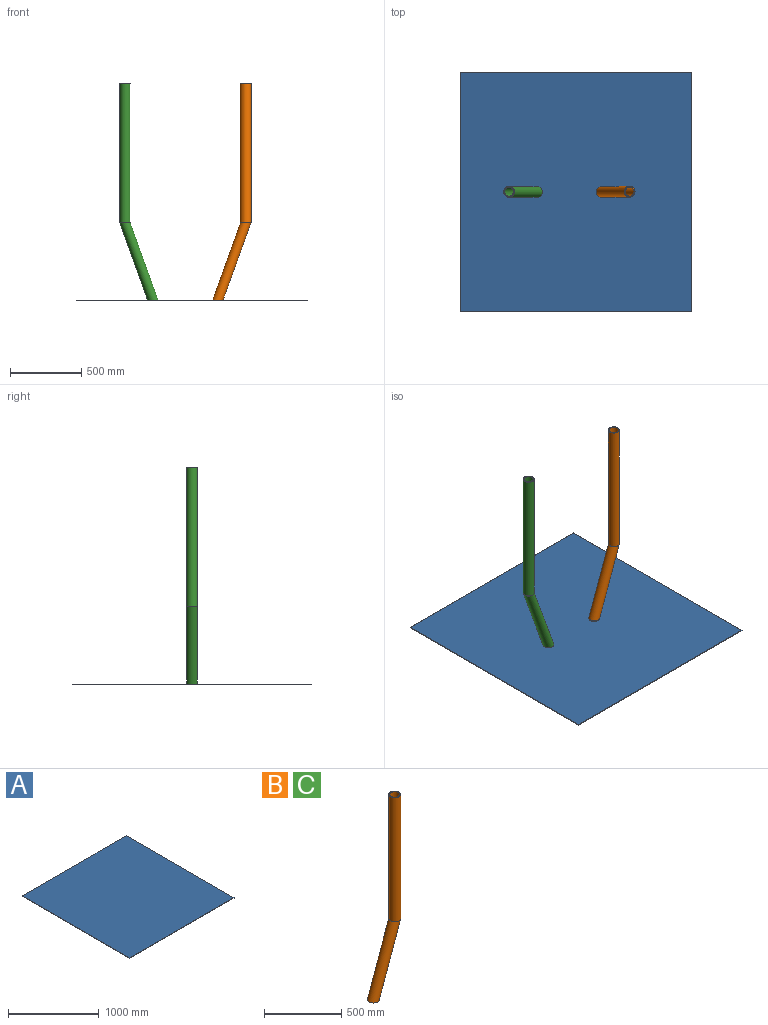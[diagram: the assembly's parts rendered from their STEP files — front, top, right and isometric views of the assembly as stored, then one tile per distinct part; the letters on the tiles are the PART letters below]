
ASSEMBLY  parts=3 mates=2
PART A: 6 faces, bbox 1625.6x1676.4x4.8 mm
  f0: plane 1625.6x4.76mm, normal (0,-1,0), area 7741.9mm2, adj f1,f3,f4,f5
  f1: plane 1676.4x4.76mm, normal (1,0,0), area 7983.9mm2, adj f0,f2,f4,f5
  f2: plane 1625.6x4.76mm, normal (0,1,0), area 7741.9mm2, adj f1,f3,f4,f5
  f3: plane 1676.4x4.76mm, normal (-1,0,0), area 7983.9mm2, adj f0,f2,f4,f5
  f4: plane 1676.4x1625.6mm, normal (0,0,1), area 2725155.8mm2, adj f0,f1,f2,f3
  f5: plane 1676.4x1625.6mm, normal (0,0,-1), area 2725155.8mm2, adj f0,f1,f2,f3
PART B: 6 faces, bbox 272.3x152.4x1524 mm
  f0: cylinder r=31.75mm len=980.44mm, axis (0,0,1), area 195589.1mm2, adj f1,f2
  f1: bspline ~543.56x259.59mm, area 112104.7mm2, adj f0,f3
  f2: plane 76.2x76.2mm, normal (0,0,1), area 1393.4mm2, adj f0,f4
  f3: plane 76.2x76.2mm, normal (0,0,-1), area 1393.4mm2, adj f1,f5
  f4: cylinder r=38.1mm len=980.44mm, axis (0,0,1), area 234706.9mm2, adj f2,f5
  f5: bspline ~543.56x272.29mm, area 134525.6mm2, adj f3,f4
PART C: same geometry as B
PLACE A at identity
PLACE B t=(-225.43,0,0)mm
PLACE C rot(axis=(0,0,1),180deg) t=(131.76,0,0)mm
MATE fastened B.f3 <-> A.f4  axis (0,0,-1) through (180.97,0,4.76)mm
MATE fastened C.f3 <-> A.f4  axis (0,0,-1) through (-274.64,0,4.76)mm
